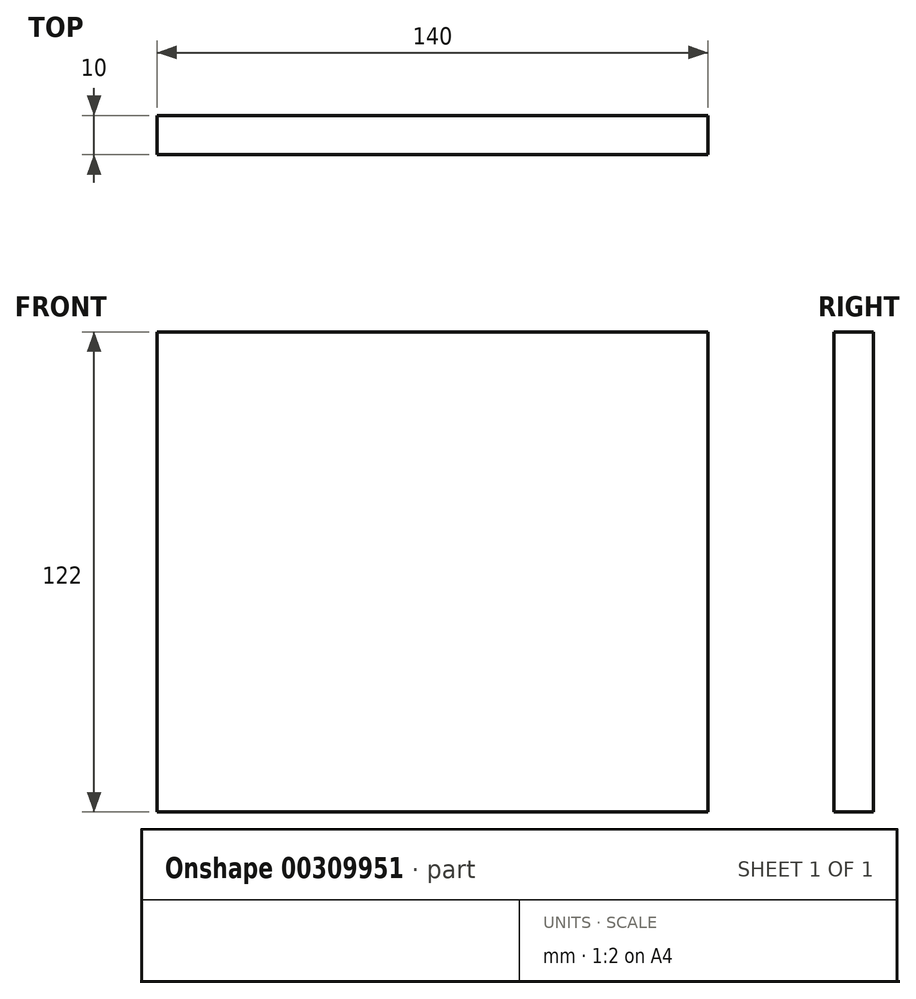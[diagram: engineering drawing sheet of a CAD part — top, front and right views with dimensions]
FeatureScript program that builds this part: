
annotation { "Feature Type Name" : "Feature", "Feature Type Description" : "" }
export const myFeature = defineFeature(function(context is Context, id is Id, definition is map)
    precondition{}
    {
        {
            var Q0;
            Q0=qCreatedBy(makeId("Front.planeOp"),FACE);
            var sketch = newSketch(context, id + "F0", { "sketchPlane" : qUnion([Q0])});
            skLineSegment(sketch, "E0.bottom", {"start": v(-72.63, 60.74) * mm, "end": v(67.37, 60.74) * mm});
            skLineSegment(sketch, "E0.top", {"start": v(-72.63, -61.26) * mm, "end": v(67.37, -61.26) * mm});
            skLineSegment(sketch, "E0.left", {"start": v(-72.63, 60.74) * mm, "end": v(-72.63, -61.26) * mm});
            skLineSegment(sketch, "E0.right", {"start": v(67.37, 60.74) * mm, "end": v(67.37, -61.26) * mm});
            skSolve(sketch);
        }
        {
            var Q0;
            Q0 = qSketchRegion(id + "F0", true);
            extrude(context, id + "F1", {"entities" : qUnion([Q0]), "depth" : 10 * mm});
        }
    });
